# Revit family: HERZ Ball Valve With Lever Handle And Check Valve 2110
name_source: partatom
category: Rohrzubehör
units: mm (PartAtom-declared; Revit-internal decimal feet)

## family parameters
Arbeitsebenenbasiert = Nein
Beim Laden mit Abzugskörper schneiden = Nein
Bemaßung runder Anschluss = Durchmesser verwenden
Gemeinsam genutzt = Nein
Immer vertikal = Ja
OmniClass-Nummer = 23.65.55.14
OmniClass-Titel = Valves for Liquid Services
Teiletyp = Unterbricht

## types (1)
- HERZ Ball Valve With Lever Handle And Check Valve 2110
    Application = HERZ ball valve with check valve is used as a shut-off valve.
The valve is used in system with potable water.
Ball valves are used when the flow of the medium has to be reilably closed.
Check valve has a function of a back-flow preventer.
    Ball = forged brass acc. to EN 12165, full bore, hollow, hard chrome plated, CW626N DZR
    Ball seals = PTFE
    Body = forged brass acc. to EN 12165, nickel plated, CW626N DZR
    Check valve O-Ring = silicon
    Check valve body = POM
    Handle = lever handle, green, steel sheet - Zn. plated
    Hersteller = HERZ Armaturen Ges.m.b.H.
    L03 = 5 mm  [stored 0.0164042 ft]
    Max. operating pressure = 2500000.0 Pa
    Max. operating temperature = 85 °C
    Medium = potable water
    Min. operating temperature = -10 °C
    Min. operating temperature (water) = 1 °C
    Note = Pursuant to Article 33 of the REACH Regulation (EC No. 1907/2006), we are obliged to point out that the material lead is listed on the SVHC list and that all brass components manufactured in our products exceed 0.1% (w / w) lead (CAS: 7439-92-1 / EINECS: 231-100-4).
Since lead is a component part of an alloy, actual exposure is not possible and therefore no additional information on safe use is necessary.
    R01 = 7 mm  [stored 0.0229659 ft]
    S04 = 5 mm  [stored 0.0164042 ft]
    SCTWCODE = 04;04;02
    SCTWSEQ = FW;SBT_TYP_FW="102";2
    SC_NennweiteBerechnet = 0
    Spindle = machined brass acc. to EB 12164, CW614N
    Spindle seals = EPDM
    Thread = acc. to ISO 228
    URL = www.herzvalves.com
    Vorgabe-Ansicht = 0 mm  [stored 0 ft]
    W01 = 45.00°

note: [stored X ft] marks values corroborated as IEEE doubles in the binary element streams (Revit-internal decimal feet)
